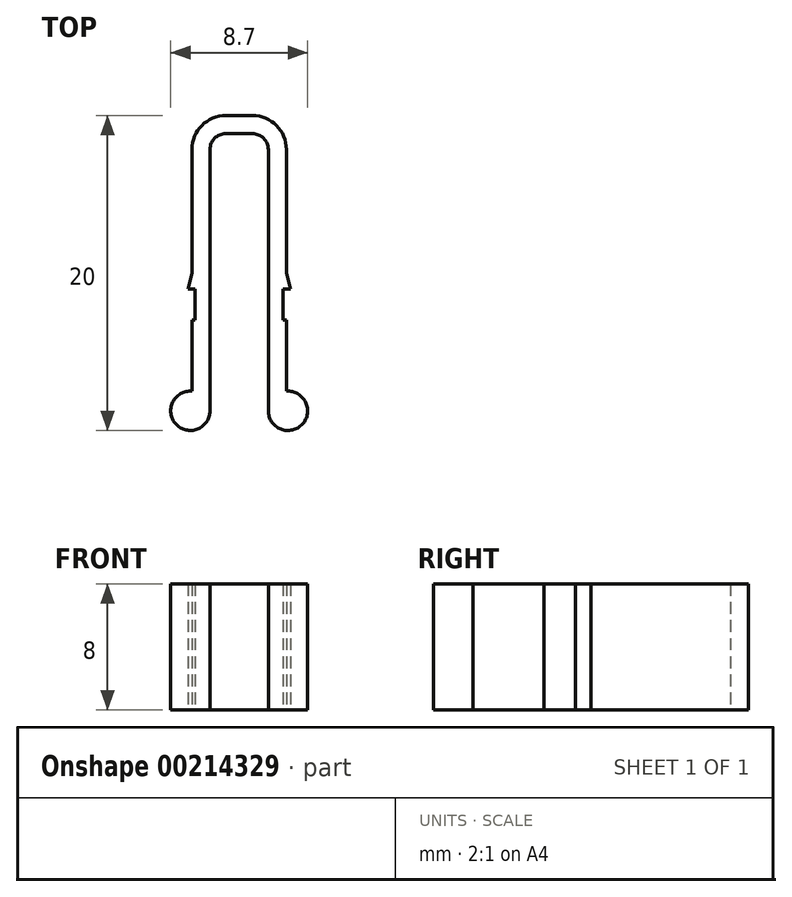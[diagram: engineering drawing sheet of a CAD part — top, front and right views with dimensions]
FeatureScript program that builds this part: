
annotation { "Feature Type Name" : "Feature", "Feature Type Description" : "" }
export const myFeature = defineFeature(function(context is Context, id is Id, definition is map)
    precondition{}
    {
        {
            var Q0;
            Q0=qCreatedBy(makeId("Top.planeOp"),FACE);
            var sketch = newSketch(context, id + "F0", { "sketchPlane" : qUnion([Q0])});
            skLineSegment(sketch, "E0", {"start": v(0, -1.15) * mm, "end": v(-0.85, -1.15) * mm});
            skLineSegment(sketch, "E1", {"start": v(-1.85, -2.15) * mm, "end": v(-1.85, -18.75) * mm});
            skArc(sketch, "E2", {"start": v(-1.85, -18.75) * mm, "mid": v(-4.02, -19.6) * mm, "end": v(-3, -17.5) * mm});
            skLineSegment(sketch, "E3", {"start": v(-3, -17.5) * mm, "end": v(-3, -13) * mm});
            skLineSegment(sketch, "E4", {"start": v(-3, -13) * mm, "end": v(-2.8, -13) * mm});
            skLineSegment(sketch, "E5", {"start": v(-2.8, -13) * mm, "end": v(-2.8, -11) * mm});
            skLineSegment(sketch, "E6", {"start": v(-2.8, -11) * mm, "end": v(-3.25, -11) * mm});
            skLineSegment(sketch, "E7", {"start": v(-3.25, -11) * mm, "end": v(-3, -10) * mm});
            skLineSegment(sketch, "E8", {"start": v(-3, -10) * mm, "end": v(-3, -2.15) * mm});
            skLineSegment(sketch, "E9", {"start": v(-0.85, 0) * mm, "end": v(0, 0) * mm});
            skLineSegment(sketch, "E10", {"start": v(0, 0) * mm, "end": v(0, -1.15) * mm});
            skLineSegment(sketch, "E11", {"start": v(-5.78, -20) * mm, "end": v(2.6, -20) * mm, "construction": true});
            skPoint(sketch, "E12.visualSharp", {"position": v(-1.85, -1.15) * mm});
            skArc(sketch, "E12.filletArc", {"start": v(-0.85, -1.15) * mm, "mid": v(-1.56, -1.44) * mm, "end": v(-1.85, -2.15) * mm});
            skPoint(sketch, "E13.visualSharp", {"position": v(-3, 0) * mm});
            skArc(sketch, "E13.filletArc", {"start": v(-0.85, 0) * mm, "mid": v(-2.37, -0.63) * mm, "end": v(-3, -2.15) * mm});
            skArc(sketch, "E14.MirrorCS", {"start": v(0.85, 0) * mm, "mid": v(2.37, -0.63) * mm, "end": v(3, -2.15) * mm});
            skLineSegment(sketch, "E15.MirrorCS", {"start": v(1.85, -2.15) * mm, "end": v(1.85, -18.75) * mm});
            skLineSegment(sketch, "E16.MirrorCS", {"start": v(3, -10) * mm, "end": v(3, -2.15) * mm});
            skPoint(sketch, "E17.MirrorP", {"position": v(1.85, -1.15) * mm});
            skLineSegment(sketch, "E18.MirrorCS", {"start": v(0, -1.15) * mm, "end": v(0.85, -1.15) * mm});
            skLineSegment(sketch, "E19.MirrorCS", {"start": v(0.85, 0) * mm, "end": v(0, 0) * mm});
            skArc(sketch, "E20.MirrorCS", {"start": v(0.85, -1.15) * mm, "mid": v(1.56, -1.44) * mm, "end": v(1.85, -2.15) * mm});
            skLineSegment(sketch, "E21.MirrorCS", {"start": v(3.25, -11) * mm, "end": v(3, -10) * mm});
            skLineSegment(sketch, "E22.MirrorCS", {"start": v(2.8, -13) * mm, "end": v(2.8, -11) * mm});
            skLineSegment(sketch, "E23.MirrorCS", {"start": v(3, -17.5) * mm, "end": v(3, -13) * mm});
            skArc(sketch, "E24.MirrorCS", {"start": v(1.85, -18.75) * mm, "mid": v(4.02, -19.6) * mm, "end": v(3, -17.5) * mm});
            skLineSegment(sketch, "E25.MirrorCS", {"start": v(3, -13) * mm, "end": v(2.8, -13) * mm});
            skLineSegment(sketch, "E26.MirrorCS", {"start": v(2.8, -11) * mm, "end": v(3.25, -11) * mm});
            skSolve(sketch);
        }
        {
            var Q0;
            Q0 = qSketchRegion(id + "F0", true);
            extrude(context, id + "F1", {"entities" : qUnion([Q0]), "endBound" : BoundingType.SYMMETRIC, "depth" : 8 * mm, "offsetDistance" : 25 * mm});
        }
    });
